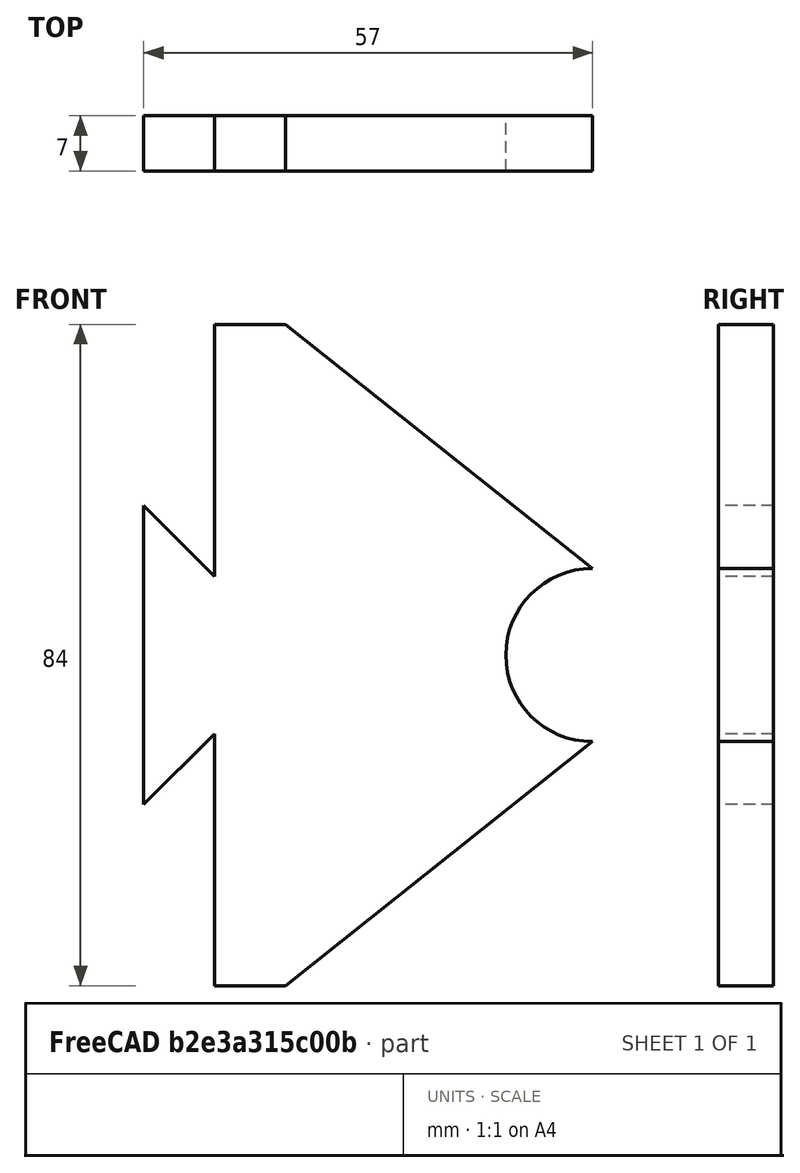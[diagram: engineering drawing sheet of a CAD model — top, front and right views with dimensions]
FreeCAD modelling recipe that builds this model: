
FCSTD DOCUMENT  (FreeCAD 0.21R33668 +26 (Git))
Label: lateral_triangular
License: All rights reserved
LicenseURL: https://en.wikipedia.org/wiki/All_rights_reserved
objects: Sketcher::SketchObject×1, PartDesign::Pad×1, PartDesign::Body×1, App::Part×1
note: 4 computed .brp shape members not serialized (recipe doc carries the construction recipe); baked Part::Feature solids carry a one-line shape summary decoded from their .brp

FEATURE [Sketcher::SketchObject] Sketch
  FullyConstrained = true
  MapMode = 5
  Placement = pos=(0,0,0) rot=(1,0,0;1.5708rad)
  Support = -> [XZ_Plane001]
  sketch-geometry (10):
    g0: LineSegment StartX=0 StartY=0 StartZ=0 EndX=9 EndY=0 EndZ=0
    g1: LineSegment StartX=9 StartY=0 StartZ=0 EndX=48 EndY=31 EndZ=0
    g2: LineSegment StartX=0 StartY=84 StartZ=0 EndX=9 EndY=84 EndZ=0
    g3: LineSegment StartX=9 StartY=84 StartZ=0 EndX=48 EndY=53 EndZ=0
    g4: ArcOfCircle CenterX=48 CenterY=42 CenterZ=0 NormalX=0 NormalY=0 NormalZ=1 AngleXU=0 Radius=11 StartAngle=1.5708 EndAngle=4.71239
    g5: LineSegment StartX=0 StartY=52 StartZ=0 EndX=-9 EndY=61 EndZ=0
    g6: LineSegment StartX=-9 StartY=61 StartZ=0 EndX=-9 EndY=23 EndZ=0
    g7: LineSegment StartX=-9 StartY=23 StartZ=0 EndX=0 EndY=32 EndZ=0
    g8: LineSegment StartX=0 StartY=52 StartZ=0 EndX=0 EndY=84 EndZ=0
    g9: LineSegment StartX=0 StartY=0 StartZ=0 EndX=0 EndY=32 EndZ=0
  constraints (30):
    c: Coincident(g0,g-1)
    c: PointOnObject(g0,g-1)
    c: Coincident(g1,g0)
    c: PointOnObject(g2,g-2)
    c: Horizontal(g2)
    c: Coincident(g3,g2)
    c: DistanceX(g0,g0) = 9
    c: DistanceX(g2,g2) = 9
    c: DistanceY(g0,g2) = 84
    c: DistanceY(g1,g3) = 22
    c: DistanceY(g0,g1) = 31
    c: DistanceX(g0,g1) = 48
    c: DistanceX(g2,g3) = 48
    c: Coincident(g4,g3)
    c: Coincident(g4,g1)
    c: Radius(g4) = 11
    c: Coincident(g6,g5)
    c: Vertical(g6)
    c: Coincident(g7,g6)
    c: DistanceY(g0,g7) = 32
    c: DistanceY(g5,g2) = 32
    c: DistanceY(g6) = 23
    c: DistanceY(g5,g2) = 23
    c: DistanceX(g5,g5) = 9
    c: Coincident(g8,g5)
    c: Coincident(g8,g2)
    c: Vertical(g8)
    c: Coincident(g9,g0)
    c: Coincident(g9,g7)
    c: Vertical(g9)
FEATURE [PartDesign::Pad] Pad
  Direction = (0,-1,2e-16)
  Length = 7
  Length2 = 10
  Placement = pos=(0,0,0) rot=(1,0,0;1.5708rad)
  Profile = -> Sketch
  ReferenceAxis = -> Sketch [N_Axis]
  Type = 0
FEATURE [PartDesign::Body] Body
  Group = -> [Sketch,Pad]
  Origin = -> Origin001
  Tip = -> Pad
FEATURE [App::Part] Part
  Group = -> [Body]
  Origin = -> Origin
